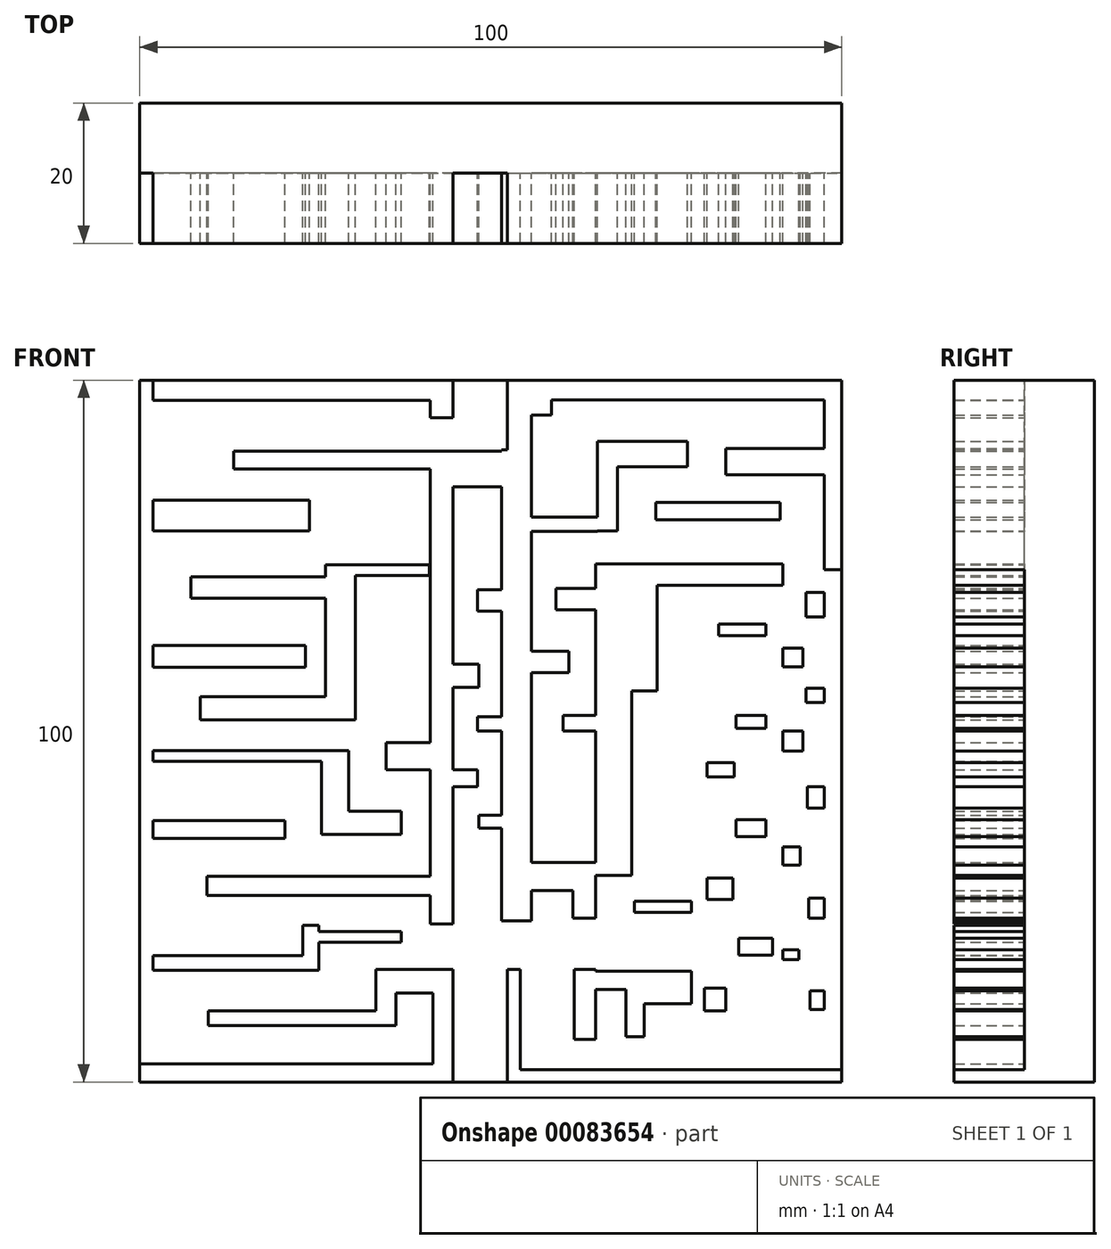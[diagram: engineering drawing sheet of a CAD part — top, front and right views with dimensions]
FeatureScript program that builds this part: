
annotation { "Feature Type Name" : "Feature", "Feature Type Description" : "" }
export const myFeature = defineFeature(function(context is Context, id is Id, definition is map)
    precondition{}
    {
        {
            var Q0;
            Q0=qCreatedBy(makeId("Front.planeOp"),FACE);
            var sketch = newSketch(context, id + "F0", { "sketchPlane" : qUnion([Q0])});
            skLineSegment(sketch, "E0.bottom", {"start": v(50, 50) * mm, "end": v(-50, 50) * mm});
            skLineSegment(sketch, "E0.top", {"start": v(50, -50) * mm, "end": v(-50, -50) * mm});
            skLineSegment(sketch, "E0.left", {"start": v(50, 50) * mm, "end": v(50, -50) * mm});
            skLineSegment(sketch, "E0.right", {"start": v(-50, 50) * mm, "end": v(-50, -50) * mm});
            skPoint(sketch, "E0.middle", {"position": v(0, 0) * mm});
            skSolve(sketch);
        }
        {
            var Q0;
            Q0=makeQuery(id+"F0.imprint","IMPRINT",FACE,{"disambiguationData":[TD([[makeQuery(id+"F0.imprint","IMPRINT",EDGE,{"derivedFrom":sQuery(id+"F0.wireOp",EDGE,"E0.bottom")}),1.0]])]});
            extrude(context, id + "F1", {"entities" : qUnion([Q0]), "depth" : 10 * mm});
        }
        {
            var Q0;
            Q0=makeQuery(id+"F1.opExtrude","CAP_FACE",FACE,{"disambiguationData":[OSD([sQuery(id+"F0.wireOp",EDGE,"E0.bottom"),sQuery(id+"F0.wireOp",EDGE,"E0.top"),sQuery(id+"F0.wireOp",EDGE,"E0.left"),sQuery(id+"F0.wireOp",EDGE,"E0.right")])],"isStart":false});
            var sketch = newSketch(context, id + "F2", { "sketchPlane" : qUnion([Q0])});
            skLineSegment(sketch, "E1.bottom", {"start": v(-5.4, -50) * mm, "end": v(-8.24, -50) * mm});
            skLineSegment(sketch, "E1.top", {"start": v(-5.4, -33.98) * mm, "end": v(-8.24, -33.98) * mm});
            skLineSegment(sketch, "E1.left", {"start": v(-5.4, -50) * mm, "end": v(-5.4, -33.98) * mm});
            skLineSegment(sketch, "E1.right", {"start": v(-8.24, -50) * mm, "end": v(-8.24, -33.98) * mm});
            skLineSegment(sketch, "E2.bottom", {"start": v(2.34, -50) * mm, "end": v(4.17, -50) * mm});
            skLineSegment(sketch, "E2.top", {"start": v(2.34, -33.98) * mm, "end": v(4.17, -33.98) * mm});
            skLineSegment(sketch, "E2.left", {"start": v(2.34, -50) * mm, "end": v(2.34, -33.98) * mm});
            skLineSegment(sketch, "E2.right", {"start": v(4.17, -50) * mm, "end": v(4.17, -33.98) * mm});
            skLineSegment(sketch, "E3.bottom", {"start": v(-5.4, -27.47) * mm, "end": v(-8.65, -27.47) * mm});
            skLineSegment(sketch, "E3.top", {"start": v(-5.4, 39.88) * mm, "end": v(-8.65, 39.88) * mm});
            skLineSegment(sketch, "E3.left", {"start": v(-5.4, -27.47) * mm, "end": v(-5.4, 39.88) * mm});
            skLineSegment(sketch, "E3.right", {"start": v(-8.65, -27.47) * mm, "end": v(-8.65, 39.88) * mm});
            skLineSegment(sketch, "E4.bottom", {"start": v(1.53, -27.06) * mm, "end": v(5.8, -27.06) * mm});
            skLineSegment(sketch, "E4.top", {"start": v(1.53, 40.09) * mm, "end": v(5.8, 40.09) * mm});
            skLineSegment(sketch, "E4.left", {"start": v(1.53, -27.06) * mm, "end": v(1.53, 40.09) * mm});
            skLineSegment(sketch, "E4.right", {"start": v(5.8, -27.06) * mm, "end": v(5.8, 40.09) * mm});
            skLineSegment(sketch, "E5.bottom", {"start": v(1.53, -13.84) * mm, "end": v(-1.73, -13.84) * mm});
            skLineSegment(sketch, "E5.top", {"start": v(1.53, -12) * mm, "end": v(-1.73, -12) * mm});
            skLineSegment(sketch, "E5.left", {"start": v(1.53, -13.84) * mm, "end": v(1.53, -12) * mm});
            skLineSegment(sketch, "E5.right", {"start": v(-1.73, -13.84) * mm, "end": v(-1.73, -12) * mm});
            skLineSegment(sketch, "E6.bottom", {"start": v(-5.4, -5.5) * mm, "end": v(-1.93, -5.5) * mm});
            skLineSegment(sketch, "E6.top", {"start": v(-5.4, -7.94) * mm, "end": v(-1.93, -7.94) * mm});
            skLineSegment(sketch, "E6.left", {"start": v(-5.4, -5.5) * mm, "end": v(-5.4, -7.94) * mm});
            skLineSegment(sketch, "E6.right", {"start": v(-1.93, -5.5) * mm, "end": v(-1.93, -7.94) * mm});
            skLineSegment(sketch, "E7.bottom", {"start": v(1.53, 0) * mm, "end": v(-1.93, 0) * mm});
            skLineSegment(sketch, "E7.top", {"start": v(1.53, 2.03) * mm, "end": v(-1.93, 2.03) * mm});
            skLineSegment(sketch, "E7.left", {"start": v(1.53, 0) * mm, "end": v(1.53, 2.03) * mm});
            skLineSegment(sketch, "E7.right", {"start": v(-1.93, 0) * mm, "end": v(-1.93, 2.03) * mm});
            skLineSegment(sketch, "E8.bottom", {"start": v(-5.4, 6.2) * mm, "end": v(-1.73, 6.2) * mm});
            skLineSegment(sketch, "E8.top", {"start": v(-5.4, 9.56) * mm, "end": v(-1.73, 9.56) * mm});
            skLineSegment(sketch, "E8.left", {"start": v(-5.4, 6.2) * mm, "end": v(-5.4, 9.56) * mm});
            skLineSegment(sketch, "E8.right", {"start": v(-1.73, 6.2) * mm, "end": v(-1.73, 9.56) * mm});
            skLineSegment(sketch, "E9.bottom", {"start": v(1.53, 17.1) * mm, "end": v(-1.93, 17.1) * mm});
            skLineSegment(sketch, "E9.top", {"start": v(1.53, 20.15) * mm, "end": v(-1.93, 20.15) * mm});
            skLineSegment(sketch, "E9.left", {"start": v(1.53, 17.1) * mm, "end": v(1.53, 20.15) * mm});
            skLineSegment(sketch, "E9.right", {"start": v(-1.93, 17.1) * mm, "end": v(-1.93, 20.15) * mm});
            skLineSegment(sketch, "E10.bottom", {"start": v(-5.4, 39.88) * mm, "end": v(1.53, 39.88) * mm});
            skLineSegment(sketch, "E10.top", {"start": v(-5.4, 34.8) * mm, "end": v(1.53, 34.8) * mm});
            skLineSegment(sketch, "E10.left", {"start": v(-5.4, 39.88) * mm, "end": v(-5.4, 34.8) * mm});
            skLineSegment(sketch, "E10.right", {"start": v(1.53, 39.88) * mm, "end": v(1.53, 34.8) * mm});
            skLineSegment(sketch, "E11.bottom", {"start": v(11.9, -33.98) * mm, "end": v(14.96, -33.98) * mm});
            skLineSegment(sketch, "E11.top", {"start": v(11.9, -43.95) * mm, "end": v(14.96, -43.95) * mm});
            skLineSegment(sketch, "E11.left", {"start": v(11.9, -33.98) * mm, "end": v(11.9, -43.95) * mm});
            skLineSegment(sketch, "E11.right", {"start": v(14.96, -33.98) * mm, "end": v(14.96, -43.95) * mm});
            skLineSegment(sketch, "E12.bottom", {"start": v(4.17, -50) * mm, "end": v(21.87, -50) * mm});
            skLineSegment(sketch, "E12.top", {"start": v(4.17, -48.23) * mm, "end": v(21.87, -48.23) * mm});
            skLineSegment(sketch, "E12.left", {"start": v(4.17, -50) * mm, "end": v(4.17, -48.23) * mm});
            skLineSegment(sketch, "E12.right", {"start": v(21.87, -50) * mm, "end": v(21.87, -48.23) * mm});
            skLineSegment(sketch, "E13.bottom", {"start": v(11.7, -26.66) * mm, "end": v(14.96, -26.66) * mm});
            skLineSegment(sketch, "E13.top", {"start": v(11.7, -18.72) * mm, "end": v(14.96, -18.72) * mm});
            skLineSegment(sketch, "E13.left", {"start": v(11.7, -26.66) * mm, "end": v(11.7, -18.72) * mm});
            skLineSegment(sketch, "E13.right", {"start": v(14.96, -26.66) * mm, "end": v(14.96, -18.72) * mm});
            skLineSegment(sketch, "E14.bottom", {"start": v(11.7, -18.72) * mm, "end": v(5.8, -18.72) * mm});
            skLineSegment(sketch, "E14.top", {"start": v(11.7, -22.69) * mm, "end": v(5.8, -22.69) * mm});
            skLineSegment(sketch, "E14.left", {"start": v(11.7, -18.72) * mm, "end": v(11.7, -22.69) * mm});
            skLineSegment(sketch, "E14.right", {"start": v(5.8, -18.72) * mm, "end": v(5.8, -22.69) * mm});
            skLineSegment(sketch, "E15.bottom", {"start": v(21.87, -43.55) * mm, "end": v(19.23, -43.55) * mm});
            skLineSegment(sketch, "E15.top", {"start": v(21.87, -34.19) * mm, "end": v(19.23, -34.19) * mm});
            skLineSegment(sketch, "E15.left", {"start": v(21.87, -43.55) * mm, "end": v(21.87, -34.19) * mm});
            skLineSegment(sketch, "E15.right", {"start": v(19.23, -43.55) * mm, "end": v(19.23, -34.19) * mm});
            skLineSegment(sketch, "E16.bottom", {"start": v(19.23, -34.19) * mm, "end": v(14.96, -34.19) * mm});
            skLineSegment(sketch, "E16.top", {"start": v(19.23, -36.83) * mm, "end": v(14.96, -36.83) * mm});
            skLineSegment(sketch, "E16.left", {"start": v(19.23, -34.19) * mm, "end": v(19.23, -36.83) * mm});
            skLineSegment(sketch, "E16.right", {"start": v(14.96, -34.19) * mm, "end": v(14.96, -36.83) * mm});
            skLineSegment(sketch, "E17.bottom", {"start": v(21.87, -50) * mm, "end": v(50, -50) * mm});
            skLineSegment(sketch, "E17.top", {"start": v(21.87, -48.23) * mm, "end": v(50, -48.23) * mm});
            skLineSegment(sketch, "E17.right", {"start": v(50, -50) * mm, "end": v(50, -48.23) * mm});
            skLineSegment(sketch, "E18.bottom", {"start": v(28.6, -48.23) * mm, "end": v(30.83, -48.23) * mm});
            skLineSegment(sketch, "E18.top", {"start": v(28.6, 6.1) * mm, "end": v(30.83, 6.1) * mm});
            skLineSegment(sketch, "E18.left", {"start": v(28.6, -48.23) * mm, "end": v(28.6, 6.1) * mm});
            skLineSegment(sketch, "E18.right", {"start": v(30.83, -48.23) * mm, "end": v(30.83, 6.1) * mm});
            skLineSegment(sketch, "E19.bottom", {"start": v(21.87, -34.19) * mm, "end": v(28.6, -34.19) * mm});
            skLineSegment(sketch, "E19.top", {"start": v(21.87, -38.87) * mm, "end": v(28.6, -38.87) * mm});
            skLineSegment(sketch, "E19.left", {"start": v(21.87, -34.19) * mm, "end": v(21.87, -38.87) * mm});
            skLineSegment(sketch, "E19.right", {"start": v(28.6, -34.19) * mm, "end": v(28.6, -38.87) * mm});
            skLineSegment(sketch, "E20.bottom", {"start": v(28.6, -24.22) * mm, "end": v(20.45, -24.22) * mm});
            skLineSegment(sketch, "E20.top", {"start": v(28.6, -25.84) * mm, "end": v(20.45, -25.84) * mm});
            skLineSegment(sketch, "E20.left", {"start": v(28.6, -24.22) * mm, "end": v(28.6, -25.84) * mm});
            skLineSegment(sketch, "E20.right", {"start": v(20.45, -24.22) * mm, "end": v(20.45, -25.84) * mm});
            skLineSegment(sketch, "E21.bottom", {"start": v(14.96, -18.72) * mm, "end": v(20.04, -18.72) * mm});
            skLineSegment(sketch, "E21.top", {"start": v(14.96, 5.7) * mm, "end": v(20.04, 5.7) * mm});
            skLineSegment(sketch, "E21.left", {"start": v(14.96, -18.72) * mm, "end": v(14.96, 5.7) * mm});
            skLineSegment(sketch, "E21.right", {"start": v(20.04, -18.72) * mm, "end": v(20.04, 5.7) * mm});
            skLineSegment(sketch, "E22.bottom", {"start": v(14.96, 5.7) * mm, "end": v(23.7, 5.7) * mm});
            skLineSegment(sketch, "E22.top", {"start": v(14.96, 23.8) * mm, "end": v(23.7, 23.8) * mm});
            skLineSegment(sketch, "E22.left", {"start": v(14.96, 5.7) * mm, "end": v(14.96, 23.8) * mm});
            skLineSegment(sketch, "E22.right", {"start": v(23.7, 5.7) * mm, "end": v(23.7, 23.8) * mm});
            skLineSegment(sketch, "E23.bottom", {"start": v(23.7, 23.8) * mm, "end": v(41.61, 23.8) * mm});
            skLineSegment(sketch, "E23.top", {"start": v(23.7, 20.76) * mm, "end": v(41.61, 20.76) * mm});
            skLineSegment(sketch, "E23.left", {"start": v(23.7, 23.8) * mm, "end": v(23.7, 20.76) * mm});
            skLineSegment(sketch, "E23.right", {"start": v(41.61, 23.8) * mm, "end": v(41.61, 20.76) * mm});
            skLineSegment(sketch, "E24.bottom", {"start": v(41.61, 20.76) * mm, "end": v(39.17, 20.76) * mm});
            skLineSegment(sketch, "E24.top", {"start": v(41.61, -41.92) * mm, "end": v(39.17, -41.92) * mm});
            skLineSegment(sketch, "E24.left", {"start": v(41.61, 20.76) * mm, "end": v(41.61, -41.92) * mm});
            skLineSegment(sketch, "E24.right", {"start": v(39.17, 20.76) * mm, "end": v(39.17, -41.92) * mm});
            skLineSegment(sketch, "E25.bottom", {"start": v(39.17, 13.63) * mm, "end": v(32.46, 13.63) * mm});
            skLineSegment(sketch, "E25.top", {"start": v(39.17, 15.26) * mm, "end": v(32.46, 15.26) * mm});
            skLineSegment(sketch, "E25.left", {"start": v(39.17, 13.63) * mm, "end": v(39.17, 15.26) * mm});
            skLineSegment(sketch, "E25.right", {"start": v(32.46, 13.63) * mm, "end": v(32.46, 15.26) * mm});
            skLineSegment(sketch, "E26.bottom", {"start": v(39.17, 0.4) * mm, "end": v(34.9, 0.4) * mm});
            skLineSegment(sketch, "E26.top", {"start": v(39.17, 2.24) * mm, "end": v(34.9, 2.24) * mm});
            skLineSegment(sketch, "E26.left", {"start": v(39.17, 0.4) * mm, "end": v(39.17, 2.24) * mm});
            skLineSegment(sketch, "E26.right", {"start": v(34.9, 0.4) * mm, "end": v(34.9, 2.24) * mm});
            skLineSegment(sketch, "E27.bottom", {"start": v(30.83, -6.51) * mm, "end": v(34.7, -6.51) * mm});
            skLineSegment(sketch, "E27.top", {"start": v(30.83, -4.48) * mm, "end": v(34.7, -4.48) * mm});
            skLineSegment(sketch, "E27.left", {"start": v(30.83, -6.51) * mm, "end": v(30.83, -4.48) * mm});
            skLineSegment(sketch, "E27.right", {"start": v(34.7, -6.51) * mm, "end": v(34.7, -4.48) * mm});
            skLineSegment(sketch, "E28.bottom", {"start": v(39.17, -15.06) * mm, "end": v(34.9, -15.06) * mm});
            skLineSegment(sketch, "E28.top", {"start": v(39.17, -12.62) * mm, "end": v(34.9, -12.62) * mm});
            skLineSegment(sketch, "E28.left", {"start": v(39.17, -15.06) * mm, "end": v(39.17, -12.62) * mm});
            skLineSegment(sketch, "E28.right", {"start": v(34.9, -15.06) * mm, "end": v(34.9, -12.62) * mm});
            skLineSegment(sketch, "E29.bottom", {"start": v(30.83, -24.01) * mm, "end": v(34.5, -24.01) * mm});
            skLineSegment(sketch, "E29.top", {"start": v(30.83, -20.96) * mm, "end": v(34.5, -20.96) * mm});
            skLineSegment(sketch, "E29.left", {"start": v(30.83, -24.01) * mm, "end": v(30.83, -20.96) * mm});
            skLineSegment(sketch, "E29.right", {"start": v(34.5, -24.01) * mm, "end": v(34.5, -20.96) * mm});
            skLineSegment(sketch, "E30.bottom", {"start": v(40.14, -31.95) * mm, "end": v(35.3, -31.95) * mm});
            skLineSegment(sketch, "E30.top", {"start": v(40.14, -29.5) * mm, "end": v(35.3, -29.5) * mm});
            skLineSegment(sketch, "E30.left", {"start": v(40.14, -31.95) * mm, "end": v(40.14, -29.5) * mm});
            skLineSegment(sketch, "E30.right", {"start": v(35.3, -31.95) * mm, "end": v(35.3, -29.5) * mm});
            skLineSegment(sketch, "E31.bottom", {"start": v(30.42, -39.88) * mm, "end": v(33.47, -39.88) * mm});
            skLineSegment(sketch, "E31.top", {"start": v(30.42, -36.63) * mm, "end": v(33.47, -36.63) * mm});
            skLineSegment(sketch, "E31.left", {"start": v(30.42, -39.88) * mm, "end": v(30.42, -36.63) * mm});
            skLineSegment(sketch, "E31.right", {"start": v(33.47, -39.88) * mm, "end": v(33.47, -36.63) * mm});
            skLineSegment(sketch, "E32.bottom", {"start": v(50, -48.23) * mm, "end": v(47.51, -48.23) * mm});
            skLineSegment(sketch, "E32.top", {"start": v(50, 23) * mm, "end": v(47.51, 23) * mm});
            skLineSegment(sketch, "E32.left", {"start": v(50, -48.23) * mm, "end": v(50, 23) * mm});
            skLineSegment(sketch, "E32.right", {"start": v(47.51, -48.23) * mm, "end": v(47.51, 23) * mm});
            skLineSegment(sketch, "E33.top", {"start": v(50, 50) * mm, "end": v(47.51, 50) * mm});
            skLineSegment(sketch, "E33.left", {"start": v(50, 23) * mm, "end": v(50, 50) * mm});
            skLineSegment(sketch, "E33.right", {"start": v(47.51, 23) * mm, "end": v(47.51, 50) * mm});
            skLineSegment(sketch, "E34.bottom", {"start": v(47.51, -37.03) * mm, "end": v(45.48, -37.03) * mm});
            skLineSegment(sketch, "E34.top", {"start": v(47.51, -39.68) * mm, "end": v(45.48, -39.68) * mm});
            skLineSegment(sketch, "E34.left", {"start": v(47.51, -37.03) * mm, "end": v(47.51, -39.68) * mm});
            skLineSegment(sketch, "E34.right", {"start": v(45.48, -37.03) * mm, "end": v(45.48, -39.68) * mm});
            skLineSegment(sketch, "E35.bottom", {"start": v(41.61, -32.56) * mm, "end": v(43.85, -32.56) * mm});
            skLineSegment(sketch, "E35.top", {"start": v(41.61, -31.13) * mm, "end": v(43.85, -31.13) * mm});
            skLineSegment(sketch, "E35.left", {"start": v(41.61, -32.56) * mm, "end": v(41.61, -31.13) * mm});
            skLineSegment(sketch, "E35.right", {"start": v(43.85, -32.56) * mm, "end": v(43.85, -31.13) * mm});
            skLineSegment(sketch, "E36.bottom", {"start": v(47.51, -26.66) * mm, "end": v(45.28, -26.66) * mm});
            skLineSegment(sketch, "E36.top", {"start": v(47.51, -23.8) * mm, "end": v(45.28, -23.8) * mm});
            skLineSegment(sketch, "E36.left", {"start": v(47.51, -26.66) * mm, "end": v(47.51, -23.8) * mm});
            skLineSegment(sketch, "E36.right", {"start": v(45.28, -26.66) * mm, "end": v(45.28, -23.8) * mm});
            skLineSegment(sketch, "E37.bottom", {"start": v(41.61, -19.13) * mm, "end": v(44.06, -19.13) * mm});
            skLineSegment(sketch, "E37.top", {"start": v(41.61, -16.48) * mm, "end": v(44.06, -16.48) * mm});
            skLineSegment(sketch, "E37.left", {"start": v(41.61, -19.13) * mm, "end": v(41.61, -16.48) * mm});
            skLineSegment(sketch, "E37.right", {"start": v(44.06, -19.13) * mm, "end": v(44.06, -16.48) * mm});
            skLineSegment(sketch, "E38.bottom", {"start": v(47.51, -10.99) * mm, "end": v(45.07, -10.99) * mm});
            skLineSegment(sketch, "E38.top", {"start": v(47.51, -7.94) * mm, "end": v(45.07, -7.94) * mm});
            skLineSegment(sketch, "E38.left", {"start": v(47.51, -10.99) * mm, "end": v(47.51, -7.94) * mm});
            skLineSegment(sketch, "E38.right", {"start": v(45.07, -10.99) * mm, "end": v(45.07, -7.94) * mm});
            skLineSegment(sketch, "E39.bottom", {"start": v(41.61, -2.85) * mm, "end": v(44.46, -2.85) * mm});
            skLineSegment(sketch, "E39.top", {"start": v(41.61, 0) * mm, "end": v(44.46, 0) * mm});
            skLineSegment(sketch, "E39.left", {"start": v(41.61, -2.85) * mm, "end": v(41.61, 0) * mm});
            skLineSegment(sketch, "E39.right", {"start": v(44.46, -2.85) * mm, "end": v(44.46, 0) * mm});
            skLineSegment(sketch, "E40.bottom", {"start": v(47.51, 6.1) * mm, "end": v(44.87, 6.1) * mm});
            skLineSegment(sketch, "E40.top", {"start": v(47.51, 4.07) * mm, "end": v(44.87, 4.07) * mm});
            skLineSegment(sketch, "E40.left", {"start": v(47.51, 6.1) * mm, "end": v(47.51, 4.07) * mm});
            skLineSegment(sketch, "E40.right", {"start": v(44.87, 6.1) * mm, "end": v(44.87, 4.07) * mm});
            skLineSegment(sketch, "E41.bottom", {"start": v(41.61, 9.16) * mm, "end": v(44.46, 9.16) * mm});
            skLineSegment(sketch, "E41.top", {"start": v(41.61, 11.8) * mm, "end": v(44.46, 11.8) * mm});
            skLineSegment(sketch, "E41.left", {"start": v(41.61, 9.16) * mm, "end": v(41.61, 11.8) * mm});
            skLineSegment(sketch, "E41.right", {"start": v(44.46, 9.16) * mm, "end": v(44.46, 11.8) * mm});
            skLineSegment(sketch, "E42.bottom", {"start": v(47.51, 16.28) * mm, "end": v(44.87, 16.28) * mm});
            skLineSegment(sketch, "E42.top", {"start": v(47.51, 19.74) * mm, "end": v(44.87, 19.74) * mm});
            skLineSegment(sketch, "E42.left", {"start": v(47.51, 16.28) * mm, "end": v(47.51, 19.74) * mm});
            skLineSegment(sketch, "E42.right", {"start": v(44.87, 16.28) * mm, "end": v(44.87, 19.74) * mm});
            skLineSegment(sketch, "E43.bottom", {"start": v(41.2, 30.12) * mm, "end": v(23.5, 30.12) * mm});
            skLineSegment(sketch, "E43.top", {"start": v(41.2, 32.56) * mm, "end": v(23.5, 32.56) * mm});
            skLineSegment(sketch, "E43.left", {"start": v(41.2, 30.12) * mm, "end": v(41.2, 32.56) * mm});
            skLineSegment(sketch, "E43.right", {"start": v(23.5, 30.12) * mm, "end": v(23.5, 32.56) * mm});
            skLineSegment(sketch, "E44.bottom", {"start": v(18, 30.52) * mm, "end": v(15.16, 30.52) * mm});
            skLineSegment(sketch, "E44.top", {"start": v(18, 41.3) * mm, "end": v(15.16, 41.3) * mm});
            skLineSegment(sketch, "E44.left", {"start": v(18, 30.52) * mm, "end": v(18, 41.3) * mm});
            skLineSegment(sketch, "E44.right", {"start": v(15.16, 30.52) * mm, "end": v(15.16, 41.3) * mm});
            skLineSegment(sketch, "E45.bottom", {"start": v(18, 41.3) * mm, "end": v(27.98, 41.3) * mm});
            skLineSegment(sketch, "E45.top", {"start": v(18, 37.65) * mm, "end": v(27.98, 37.65) * mm});
            skLineSegment(sketch, "E45.left", {"start": v(18, 41.3) * mm, "end": v(18, 37.65) * mm});
            skLineSegment(sketch, "E45.right", {"start": v(27.98, 41.3) * mm, "end": v(27.98, 37.65) * mm});
            skLineSegment(sketch, "E46.bottom", {"start": v(27.98, 37.65) * mm, "end": v(26.35, 37.65) * mm});
            skLineSegment(sketch, "E46.top", {"start": v(27.98, 32.56) * mm, "end": v(26.35, 32.56) * mm});
            skLineSegment(sketch, "E46.left", {"start": v(27.98, 37.65) * mm, "end": v(27.98, 32.56) * mm});
            skLineSegment(sketch, "E46.right", {"start": v(26.35, 37.65) * mm, "end": v(26.35, 32.56) * mm});
            skLineSegment(sketch, "E47.bottom", {"start": v(15.16, 30.52) * mm, "end": v(5.8, 30.52) * mm});
            skLineSegment(sketch, "E47.top", {"start": v(15.16, 28.49) * mm, "end": v(5.8, 28.49) * mm});
            skLineSegment(sketch, "E47.left", {"start": v(15.16, 30.52) * mm, "end": v(15.16, 28.49) * mm});
            skLineSegment(sketch, "E47.right", {"start": v(5.8, 30.52) * mm, "end": v(5.8, 28.49) * mm});
            skLineSegment(sketch, "E48.bottom", {"start": v(14.96, 20.35) * mm, "end": v(9.26, 20.35) * mm});
            skLineSegment(sketch, "E48.top", {"start": v(14.96, 17.3) * mm, "end": v(9.26, 17.3) * mm});
            skLineSegment(sketch, "E48.left", {"start": v(14.96, 20.35) * mm, "end": v(14.96, 17.3) * mm});
            skLineSegment(sketch, "E48.right", {"start": v(9.26, 20.35) * mm, "end": v(9.26, 17.3) * mm});
            skLineSegment(sketch, "E49.bottom", {"start": v(5.8, 11.4) * mm, "end": v(11.1, 11.4) * mm});
            skLineSegment(sketch, "E49.top", {"start": v(5.8, 8.34) * mm, "end": v(11.1, 8.34) * mm});
            skLineSegment(sketch, "E49.left", {"start": v(5.8, 11.4) * mm, "end": v(5.8, 8.34) * mm});
            skLineSegment(sketch, "E49.right", {"start": v(11.1, 11.4) * mm, "end": v(11.1, 8.34) * mm});
            skLineSegment(sketch, "E50.bottom", {"start": v(14.96, 0) * mm, "end": v(10.28, 0) * mm});
            skLineSegment(sketch, "E50.top", {"start": v(14.96, 2.24) * mm, "end": v(10.28, 2.24) * mm});
            skLineSegment(sketch, "E50.left", {"start": v(14.96, 0) * mm, "end": v(14.96, 2.24) * mm});
            skLineSegment(sketch, "E50.right", {"start": v(10.28, 0) * mm, "end": v(10.28, 2.24) * mm});
            skLineSegment(sketch, "E51.bottom", {"start": v(47.51, 40.3) * mm, "end": v(33.47, 40.3) * mm});
            skLineSegment(sketch, "E51.top", {"start": v(47.51, 36.5) * mm, "end": v(33.47, 36.5) * mm});
            skLineSegment(sketch, "E51.left", {"start": v(47.51, 40.3) * mm, "end": v(47.51, 36.5) * mm});
            skLineSegment(sketch, "E51.right", {"start": v(33.47, 40.3) * mm, "end": v(33.47, 36.5) * mm});
            skLineSegment(sketch, "E52.bottom", {"start": v(47.51, 50) * mm, "end": v(8.65, 50) * mm});
            skLineSegment(sketch, "E52.top", {"start": v(47.51, 47.2) * mm, "end": v(8.65, 47.2) * mm});
            skLineSegment(sketch, "E52.left", {"start": v(47.51, 50) * mm, "end": v(47.51, 47.2) * mm});
            skLineSegment(sketch, "E52.right", {"start": v(8.65, 50) * mm, "end": v(8.65, 47.2) * mm});
            skLineSegment(sketch, "E53.bottom", {"start": v(2.34, 50) * mm, "end": v(5.8, 50) * mm});
            skLineSegment(sketch, "E53.top", {"start": v(2.34, 40.09) * mm, "end": v(5.8, 40.09) * mm});
            skLineSegment(sketch, "E53.left", {"start": v(2.34, 50) * mm, "end": v(2.34, 40.09) * mm});
            skLineSegment(sketch, "E53.right", {"start": v(5.8, 50) * mm, "end": v(5.8, 40.09) * mm});
            skLineSegment(sketch, "E54.bottom", {"start": v(8.65, 50) * mm, "end": v(5.8, 50) * mm});
            skLineSegment(sketch, "E54.top", {"start": v(8.65, 45.04) * mm, "end": v(5.8, 45.04) * mm});
            skLineSegment(sketch, "E54.left", {"start": v(8.65, 50) * mm, "end": v(8.65, 45.04) * mm});
            skLineSegment(sketch, "E54.right", {"start": v(5.8, 50) * mm, "end": v(5.8, 45.04) * mm});
            skLineSegment(sketch, "E55.bottom", {"start": v(-8.24, -50) * mm, "end": v(-50, -50) * mm});
            skLineSegment(sketch, "E55.top", {"start": v(-8.24, -47.41) * mm, "end": v(-50, -47.41) * mm});
            skLineSegment(sketch, "E55.left", {"start": v(-8.24, -50) * mm, "end": v(-8.24, -47.41) * mm});
            skLineSegment(sketch, "E55.right", {"start": v(-50, -50) * mm, "end": v(-50, -47.41) * mm});
            skLineSegment(sketch, "E56.bottom", {"start": v(-50, -47.41) * mm, "end": v(-48.13, -47.41) * mm});
            skLineSegment(sketch, "E56.top", {"start": v(-50, 50) * mm, "end": v(-48.13, 50) * mm});
            skLineSegment(sketch, "E56.left", {"start": v(-50, -47.41) * mm, "end": v(-50, 50) * mm});
            skLineSegment(sketch, "E56.right", {"start": v(-48.13, -47.41) * mm, "end": v(-48.13, 50) * mm});
            skPoint(sketch, "E57.oppositeSnap0", {"position": v(-8.24, -42) * mm});
            skLineSegment(sketch, "E57.bottom", {"start": v(-13.53, -33.98) * mm, "end": v(-16.38, -33.98) * mm});
            skLineSegment(sketch, "E57.top", {"start": v(-13.53, -42) * mm, "end": v(-16.38, -42) * mm});
            skLineSegment(sketch, "E57.left", {"start": v(-13.53, -33.98) * mm, "end": v(-13.53, -42) * mm});
            skLineSegment(sketch, "E57.right", {"start": v(-16.38, -33.98) * mm, "end": v(-16.38, -42) * mm});
            skLineSegment(sketch, "E58.bottom", {"start": v(-16.38, -42) * mm, "end": v(-40.25, -42) * mm});
            skLineSegment(sketch, "E58.top", {"start": v(-16.38, -39.86) * mm, "end": v(-40.25, -39.86) * mm});
            skLineSegment(sketch, "E58.left", {"start": v(-16.38, -42) * mm, "end": v(-16.38, -39.86) * mm});
            skLineSegment(sketch, "E58.right", {"start": v(-40.25, -42) * mm, "end": v(-40.25, -39.86) * mm});
            skLineSegment(sketch, "E59.bottom", {"start": v(-48.13, -31.99) * mm, "end": v(-26.8, -31.99) * mm});
            skLineSegment(sketch, "E59.top", {"start": v(-48.13, -34.1) * mm, "end": v(-26.8, -34.1) * mm});
            skLineSegment(sketch, "E59.left", {"start": v(-48.13, -31.99) * mm, "end": v(-48.13, -34.1) * mm});
            skLineSegment(sketch, "E60.top", {"start": v(-26.8, -27.68) * mm, "end": v(-24.5, -27.68) * mm});
            skLineSegment(sketch, "E60.left", {"start": v(-26.8, -31.99) * mm, "end": v(-26.8, -27.68) * mm});
            skLineSegment(sketch, "E60.right", {"start": v(-24.5, -31.99) * mm, "end": v(-24.5, -30.07) * mm});
            skLineSegment(sketch, "E61.bottom", {"start": v(-24.5, -28.53) * mm, "end": v(-12.79, -28.53) * mm});
            skLineSegment(sketch, "E61.top", {"start": v(-24.5, -30.07) * mm, "end": v(-12.79, -30.07) * mm});
            skLineSegment(sketch, "E61.right", {"start": v(-12.79, -28.53) * mm, "end": v(-12.79, -30.07) * mm});
            skLineSegment(sketch, "E62.bottom", {"start": v(-8.65, -20.66) * mm, "end": v(-40.44, -20.66) * mm});
            skLineSegment(sketch, "E62.top", {"start": v(-8.65, -23.44) * mm, "end": v(-40.44, -23.44) * mm});
            skLineSegment(sketch, "E62.left", {"start": v(-8.65, -20.66) * mm, "end": v(-8.65, -23.44) * mm});
            skLineSegment(sketch, "E62.right", {"start": v(-40.44, -20.66) * mm, "end": v(-40.44, -23.44) * mm});
            skLineSegment(sketch, "E63.bottom", {"start": v(-48.13, -12.78) * mm, "end": v(-29.3, -12.78) * mm});
            skLineSegment(sketch, "E63.top", {"start": v(-48.13, -15.28) * mm, "end": v(-29.3, -15.28) * mm});
            skLineSegment(sketch, "E63.left", {"start": v(-48.13, -12.78) * mm, "end": v(-48.13, -15.28) * mm});
            skLineSegment(sketch, "E63.right", {"start": v(-29.3, -12.78) * mm, "end": v(-29.3, -15.28) * mm});
            skLineSegment(sketch, "E64.bottom", {"start": v(-24.12, -14.7) * mm, "end": v(-20.28, -14.7) * mm});
            skLineSegment(sketch, "E64.top", {"start": v(-24.12, -2.8) * mm, "end": v(-20.28, -2.8) * mm});
            skLineSegment(sketch, "E64.left", {"start": v(-24.12, -14.7) * mm, "end": v(-24.12, -2.8) * mm});
            skLineSegment(sketch, "E64.right", {"start": v(-20.28, -14.7) * mm, "end": v(-20.28, -2.8) * mm});
            skLineSegment(sketch, "E65.bottom", {"start": v(-24.12, -2.8) * mm, "end": v(-48.13, -2.8) * mm});
            skLineSegment(sketch, "E65.top", {"start": v(-24.12, -4.33) * mm, "end": v(-48.13, -4.33) * mm});
            skLineSegment(sketch, "E65.left", {"start": v(-24.12, -2.8) * mm, "end": v(-24.12, -4.33) * mm});
            skLineSegment(sketch, "E65.right", {"start": v(-48.13, -2.8) * mm, "end": v(-48.13, -4.33) * mm});
            skLineSegment(sketch, "E66.bottom", {"start": v(-20.28, -14.7) * mm, "end": v(-12.79, -14.7) * mm});
            skLineSegment(sketch, "E66.top", {"start": v(-20.28, -11.44) * mm, "end": v(-12.79, -11.44) * mm});
            skLineSegment(sketch, "E66.left", {"start": v(-20.28, -14.7) * mm, "end": v(-20.28, -11.44) * mm});
            skLineSegment(sketch, "E66.right", {"start": v(-12.79, -14.7) * mm, "end": v(-12.79, -11.44) * mm});
            skLineSegment(sketch, "E67.bottom", {"start": v(-8.65, -1.64) * mm, "end": v(-14.9, -1.64) * mm});
            skLineSegment(sketch, "E67.top", {"start": v(-8.65, -5.48) * mm, "end": v(-14.9, -5.48) * mm});
            skLineSegment(sketch, "E67.left", {"start": v(-8.65, -1.64) * mm, "end": v(-8.65, -5.48) * mm});
            skLineSegment(sketch, "E67.right", {"start": v(-14.9, -1.64) * mm, "end": v(-14.9, -5.48) * mm});
            skLineSegment(sketch, "E68.bottom", {"start": v(-14.9, -1.64) * mm, "end": v(-12.98, -1.64) * mm});
            skLineSegment(sketch, "E68.top", {"start": v(-14.9, 17.18) * mm, "end": v(-12.98, 17.18) * mm});
            skLineSegment(sketch, "E68.left", {"start": v(-14.9, -1.64) * mm, "end": v(-14.9, 17.18) * mm});
            skLineSegment(sketch, "E68.right", {"start": v(-12.98, -1.64) * mm, "end": v(-12.98, 17.18) * mm});
            skLineSegment(sketch, "E69.bottom", {"start": v(-8.75, 23.71) * mm, "end": v(-19.32, 23.71) * mm});
            skLineSegment(sketch, "E69.top", {"start": v(-8.75, 22.17) * mm, "end": v(-19.32, 22.17) * mm});
            skLineSegment(sketch, "E69.left", {"start": v(-8.75, 23.71) * mm, "end": v(-8.75, 22.17) * mm});
            skLineSegment(sketch, "E69.right", {"start": v(-19.32, 23.71) * mm, "end": v(-19.32, 22.17) * mm});
            skLineSegment(sketch, "E70.bottom", {"start": v(-19.32, 23.71) * mm, "end": v(-23.54, 23.71) * mm});
            skLineSegment(sketch, "E70.top", {"start": v(-19.32, 4.89) * mm, "end": v(-23.54, 4.89) * mm});
            skLineSegment(sketch, "E70.left", {"start": v(-19.32, 23.71) * mm, "end": v(-19.32, 4.89) * mm});
            skLineSegment(sketch, "E70.right", {"start": v(-23.54, 23.71) * mm, "end": v(-23.54, 4.89) * mm});
            skLineSegment(sketch, "E71.bottom", {"start": v(-23.54, 4.89) * mm, "end": v(-41.4, 4.89) * mm});
            skLineSegment(sketch, "E71.top", {"start": v(-23.54, 1.62) * mm, "end": v(-41.4, 1.62) * mm});
            skLineSegment(sketch, "E71.left", {"start": v(-23.54, 4.89) * mm, "end": v(-23.54, 1.62) * mm});
            skLineSegment(sketch, "E71.right", {"start": v(-41.4, 4.89) * mm, "end": v(-41.4, 1.62) * mm});
            skLineSegment(sketch, "E72.bottom", {"start": v(-48.13, 12.19) * mm, "end": v(-26.42, 12.19) * mm});
            skLineSegment(sketch, "E72.top", {"start": v(-48.13, 9.11) * mm, "end": v(-26.42, 9.11) * mm});
            skLineSegment(sketch, "E72.left", {"start": v(-48.13, 12.19) * mm, "end": v(-48.13, 9.11) * mm});
            skLineSegment(sketch, "E72.right", {"start": v(-26.42, 12.19) * mm, "end": v(-26.42, 9.11) * mm});
            skLineSegment(sketch, "E73.bottom", {"start": v(-23.54, 21.98) * mm, "end": v(-42.75, 21.98) * mm});
            skLineSegment(sketch, "E73.top", {"start": v(-23.54, 18.9) * mm, "end": v(-42.75, 18.9) * mm});
            skLineSegment(sketch, "E73.left", {"start": v(-23.54, 21.98) * mm, "end": v(-23.54, 18.9) * mm});
            skLineSegment(sketch, "E73.right", {"start": v(-42.75, 21.98) * mm, "end": v(-42.75, 18.9) * mm});
            skLineSegment(sketch, "E74.bottom", {"start": v(-48.13, 32.93) * mm, "end": v(-25.85, 32.93) * mm});
            skLineSegment(sketch, "E74.top", {"start": v(-48.13, 28.51) * mm, "end": v(-25.85, 28.51) * mm});
            skLineSegment(sketch, "E74.left", {"start": v(-48.13, 32.93) * mm, "end": v(-48.13, 28.51) * mm});
            skLineSegment(sketch, "E74.right", {"start": v(-25.85, 32.93) * mm, "end": v(-25.85, 28.51) * mm});
            skLineSegment(sketch, "E75.bottom", {"start": v(-5.4, 50) * mm, "end": v(-8.65, 50) * mm});
            skLineSegment(sketch, "E75.top", {"start": v(-5.4, 44.65) * mm, "end": v(-8.65, 44.65) * mm});
            skLineSegment(sketch, "E75.left", {"start": v(-5.4, 50) * mm, "end": v(-5.4, 44.65) * mm});
            skLineSegment(sketch, "E75.right", {"start": v(-8.65, 50) * mm, "end": v(-8.65, 44.65) * mm});
            skLineSegment(sketch, "E76.bottom", {"start": v(-8.65, 50) * mm, "end": v(-48.13, 50) * mm});
            skLineSegment(sketch, "E76.top", {"start": v(-8.65, 47.14) * mm, "end": v(-48.13, 47.14) * mm});
            skLineSegment(sketch, "E76.left", {"start": v(-8.65, 50) * mm, "end": v(-8.65, 47.14) * mm});
            skLineSegment(sketch, "E76.right", {"start": v(-48.13, 50) * mm, "end": v(-48.13, 47.14) * mm});
            skLineSegment(sketch, "E77.bottom", {"start": v(-8.65, 39.88) * mm, "end": v(-36.6, 39.88) * mm});
            skLineSegment(sketch, "E77.top", {"start": v(-8.65, 37.35) * mm, "end": v(-36.6, 37.35) * mm});
            skLineSegment(sketch, "E77.left", {"start": v(-8.65, 39.88) * mm, "end": v(-8.65, 37.35) * mm});
            skLineSegment(sketch, "E77.right", {"start": v(-36.6, 39.88) * mm, "end": v(-36.6, 37.35) * mm});
            skLineSegment(sketch, "E78.bottom", {"start": v(-19.32, 23.71) * mm, "end": v(-15.28, 23.71) * mm});
            skLineSegment(sketch, "E78.top", {"start": v(-19.32, 32.74) * mm, "end": v(-15.28, 32.74) * mm});
            skLineSegment(sketch, "E78.left", {"start": v(-19.32, 23.71) * mm, "end": v(-19.32, 32.74) * mm});
            skLineSegment(sketch, "E78.right", {"start": v(-15.28, 23.71) * mm, "end": v(-15.28, 32.74) * mm});
            skLineSegment(sketch, "E79.bottom", {"start": v(-42.56, 32.93) * mm, "end": v(-41.02, 32.93) * mm});
            skLineSegment(sketch, "E79.top", {"start": v(-42.56, 42.34) * mm, "end": v(-41.02, 42.34) * mm});
            skLineSegment(sketch, "E79.left", {"start": v(-42.56, 32.93) * mm, "end": v(-42.56, 42.34) * mm});
            skLineSegment(sketch, "E79.right", {"start": v(-41.02, 32.93) * mm, "end": v(-41.02, 42.34) * mm});
            skLineSegment(sketch, "E80.bottom", {"start": v(-13.53, -33.98) * mm, "end": v(-8.24, -33.98) * mm});
            skLineSegment(sketch, "E80.top", {"start": v(-13.53, -37.3) * mm, "end": v(-8.24, -37.3) * mm});
            skLineSegment(sketch, "E80.left", {"start": v(-13.53, -33.98) * mm, "end": v(-13.53, -37.3) * mm});
            skLineSegment(sketch, "E80.right", {"start": v(-8.24, -33.98) * mm, "end": v(-8.24, -37.3) * mm});
            skLineSegment(sketch, "E81.bottom", {"start": v(-23.54, 1.62) * mm, "end": v(-19.32, 1.62) * mm});
            skLineSegment(sketch, "E81.top", {"start": v(-23.54, 4.89) * mm, "end": v(-19.32, 4.89) * mm});
            skLineSegment(sketch, "E81.left", {"start": v(-23.54, 1.62) * mm, "end": v(-23.54, 4.89) * mm});
            skLineSegment(sketch, "E81.right", {"start": v(-19.32, 1.62) * mm, "end": v(-19.32, 4.89) * mm});
            skLineSegment(sketch, "E82", {"start": v(-24.5, -31.99) * mm, "end": v(-24.5, -34.1) * mm});
            skLineSegment(sketch, "E83", {"start": v(-24.5, -34.1) * mm, "end": v(-26.8, -34.1) * mm});
            skLineSegment(sketch, "E84.bottom", {"start": v(15.16, 30.52) * mm, "end": v(18, 30.52) * mm});
            skLineSegment(sketch, "E84.top", {"start": v(15.16, 28.5) * mm, "end": v(18, 28.5) * mm});
            skLineSegment(sketch, "E84.left", {"start": v(15.16, 30.52) * mm, "end": v(15.16, 28.5) * mm});
            skLineSegment(sketch, "E84.right", {"start": v(18, 30.52) * mm, "end": v(18, 28.5) * mm});
            skLineSegment(sketch, "E85.trimOffspring", {"start": v(-24.5, -28.53) * mm, "end": v(-24.5, -27.68) * mm});
            skLineSegment(sketch, "E86.bottom", {"start": v(14.96, -20.57) * mm, "end": v(20.04, -20.57) * mm});
            skLineSegment(sketch, "E86.left", {"start": v(14.96, -20.57) * mm, "end": v(14.96, -18.72) * mm});
            skLineSegment(sketch, "E86.right", {"start": v(20.04, -20.57) * mm, "end": v(20.04, -18.72) * mm});
            skSolve(sketch);
        }
        {
            var Q0;
            Q0=makeQuery(id+"F2.imprint","IMPRINT",FACE,{"disambiguationData":[TD([[makeQuery(id+"F2.imprint","IMPRINT",EDGE,{"derivedFrom":sQuery(id+"F2.wireOp",EDGE,"E59.bottom")}),-1.0]])]});
            var Q1;
            Q1=makeQuery(id+"F2.imprint","IMPRINT",FACE,{"disambiguationData":[TD([[makeQuery(id+"F2.imprint","IMPRINT",EDGE,{"derivedFrom":sQuery(id+"F2.wireOp",EDGE,"E58.bottom")}),-1.0]])]});
            var Q2;
            Q2=makeQuery(id+"F2.imprint","IMPRINT",FACE,{"disambiguationData":[TD([[makeQuery(id+"F2.imprint","IMPRINT",EDGE,{"derivedFrom":sQuery(id+"F2.wireOp",EDGE,"E55.bottom")}),-1.0]])]});
            var Q3;
            {var subQ7=sQuery(id+"F2.wireOp",EDGE,"E56.bottom");Q3=makeQuery(id+"F2.imprint","IMPRINT",FACE,{"disambiguationData":[TD([[makeQuery(id+"F2.imprint","IMPRINT",EDGE,{"derivedFrom":subQ7}),1.0]])]});}
            var Q4;
            Q4=makeQuery(id+"F2.imprint","IMPRINT",FACE,{"disambiguationData":[TD([[makeQuery(id+"F2.imprint","IMPRINT",EDGE,{"derivedFrom":sQuery(id+"F2.wireOp",EDGE,"E76.bottom")}),1.0]])]});
            var Q5;
            Q5=makeQuery(id+"F2.imprint","IMPRINT",FACE,{"disambiguationData":[TD([[makeQuery(id+"F2.imprint","IMPRINT",EDGE,{"derivedFrom":sQuery(id+"F2.wireOp",EDGE,"E75.bottom")}),1.0]])]});
            var Q6;
            Q6=makeQuery(id+"F2.imprint","IMPRINT",FACE,{"disambiguationData":[TD([[makeQuery(id+"F2.imprint","IMPRINT",EDGE,{"derivedFrom":sQuery(id+"F2.wireOp",EDGE,"E53.bottom")}),1.0]])]});
            var Q7;
            {var subQ3=sQuery(id+"F2.wireOp",EDGE,"E54.bottom");Q7=makeQuery(id+"F2.imprint","IMPRINT",FACE,{"disambiguationData":[TD([[makeQuery(id+"F2.imprint","IMPRINT",EDGE,{"derivedFrom":subQ3}),1.0]])]});}
            var Q8;
            {var subQ0=sQuery(id+"F2.wireOp",EDGE,"E52.bottom");Q8=makeQuery(id+"F2.imprint","IMPRINT",FACE,{"disambiguationData":[TD([[makeQuery(id+"F2.imprint","IMPRINT",EDGE,{"derivedFrom":subQ0}),1.0]])]});}
            var Q9;
            {var subQ0=sQuery(id+"F2.wireOp",EDGE,"E32.top");Q9=makeQuery(id+"F2.imprint","IMPRINT",FACE,{"disambiguationData":[TD([[makeQuery(id+"F2.imprint","IMPRINT",EDGE,{"derivedFrom":subQ0}),-1.0]])]});}
            var Q10;
            {var subQ6=sQuery(id+"F2.wireOp",EDGE,"E32.bottom");Q10=makeQuery(id+"F2.imprint","IMPRINT",FACE,{"disambiguationData":[TD([[makeQuery(id+"F2.imprint","IMPRINT",EDGE,{"derivedFrom":subQ6}),-1.0]])]});}
            var Q11;
            Q11=makeQuery(id+"F2.imprint","IMPRINT",FACE,{"disambiguationData":[TD([[makeQuery(id+"F2.imprint","IMPRINT",EDGE,{"derivedFrom":sQuery(id+"F2.wireOp",EDGE,"E17.bottom")}),-1.0]])]});
            var Q12;
            Q12=makeQuery(id+"F2.imprint","IMPRINT",FACE,{"disambiguationData":[TD([[makeQuery(id+"F2.imprint","IMPRINT",EDGE,{"derivedFrom":sQuery(id+"F2.wireOp",EDGE,"E12.bottom")}),-1.0]])]});
            var Q13;
            Q13=makeQuery(id+"F2.imprint","IMPRINT",FACE,{"disambiguationData":[TD([[makeQuery(id+"F2.imprint","IMPRINT",EDGE,{"derivedFrom":sQuery(id+"F2.wireOp",EDGE,"E2.bottom")}),-1.0]])]});
            var Q14;
            Q14=makeQuery(id+"F2.imprint","IMPRINT",FACE,{"disambiguationData":[TD([[makeQuery(id+"F2.imprint","IMPRINT",EDGE,{"derivedFrom":sQuery(id+"F2.wireOp",EDGE,"E1.bottom")}),-1.0]])]});
            var Q15;
            Q15=makeQuery(id+"F2.imprint","IMPRINT",FACE,{"disambiguationData":[TD([[makeQuery(id+"F2.imprint","IMPRINT",EDGE,{"derivedFrom":sQuery(id+"F2.wireOp",EDGE,"E80.bottom")}),-1.0]])]});
            var Q16;
            Q16=makeQuery(id+"F2.imprint","IMPRINT",FACE,{"disambiguationData":[TD([[makeQuery(id+"F2.imprint","IMPRINT",EDGE,{"derivedFrom":sQuery(id+"F2.wireOp",EDGE,"E57.bottom")}),1.0]])]});
            var Q17;
            Q17=makeQuery(id+"F2.imprint","IMPRINT",FACE,{"disambiguationData":[TD([[makeQuery(id+"F2.imprint","IMPRINT",EDGE,{"derivedFrom":sQuery(id+"F2.wireOp",EDGE,"E63.bottom")}),-1.0]])]});
            var Q18;
            Q18=makeQuery(id+"F2.imprint","IMPRINT",FACE,{"disambiguationData":[TD([[makeQuery(id+"F2.imprint","IMPRINT",EDGE,{"derivedFrom":sQuery(id+"F2.wireOp",EDGE,"E65.bottom")}),1.0]])]});
            var Q19;
            Q19=makeQuery(id+"F2.imprint","IMPRINT",FACE,{"disambiguationData":[TD([[makeQuery(id+"F2.imprint","IMPRINT",EDGE,{"derivedFrom":sQuery(id+"F2.wireOp",EDGE,"E64.bottom")}),1.0]])]});
            var Q20;
            Q20=makeQuery(id+"F2.imprint","IMPRINT",FACE,{"disambiguationData":[TD([[makeQuery(id+"F2.imprint","IMPRINT",EDGE,{"derivedFrom":sQuery(id+"F2.wireOp",EDGE,"E66.bottom")}),1.0]])]});
            var Q21;
            Q21=makeQuery(id+"F2.imprint","IMPRINT",FACE,{"disambiguationData":[TD([[makeQuery(id+"F2.imprint","IMPRINT",EDGE,{"derivedFrom":sQuery(id+"F2.wireOp",EDGE,"E72.bottom")}),-1.0]])]});
            var Q22;
            Q22=makeQuery(id+"F2.imprint","IMPRINT",FACE,{"disambiguationData":[TD([[makeQuery(id+"F2.imprint","IMPRINT",EDGE,{"derivedFrom":sQuery(id+"F2.wireOp",EDGE,"E74.top")}),1.0]])]});
            var Q23;
            Q23=makeQuery(id+"F2.imprint","IMPRINT",FACE,{"disambiguationData":[TD([[makeQuery(id+"F2.imprint","IMPRINT",EDGE,{"derivedFrom":sQuery(id+"F2.wireOp",EDGE,"E79.bottom")}),1.0]])]});
            var Q24;
            {var subQ3=sQuery(id+"F2.wireOp",EDGE,"E4.bottom");Q24=makeQuery(id+"F2.imprint","IMPRINT",FACE,{"disambiguationData":[TD([[makeQuery(id+"F2.imprint","IMPRINT",EDGE,{"derivedFrom":subQ3}),1.0]])]});}
            var Q25;
            Q25=makeQuery(id+"F2.imprint","IMPRINT",FACE,{"disambiguationData":[TD([[makeQuery(id+"F2.imprint","IMPRINT",EDGE,{"derivedFrom":sQuery(id+"F2.wireOp",EDGE,"E10.bottom")}),-1.0]])]});
            var Q26;
            {var subQ6=sQuery(id+"F2.wireOp",EDGE,"E3.bottom");Q26=makeQuery(id+"F2.imprint","IMPRINT",FACE,{"disambiguationData":[TD([[makeQuery(id+"F2.imprint","IMPRINT",EDGE,{"derivedFrom":subQ6}),-1.0]])]});}
            var Q27;
            Q27=makeQuery(id+"F2.imprint","IMPRINT",FACE,{"disambiguationData":[TD([[makeQuery(id+"F2.imprint","IMPRINT",EDGE,{"derivedFrom":sQuery(id+"F2.wireOp",EDGE,"E77.bottom")}),1.0]])]});
            var Q28;
            Q28=makeQuery(id+"F2.imprint","IMPRINT",FACE,{"disambiguationData":[TD([[makeQuery(id+"F2.imprint","IMPRINT",EDGE,{"derivedFrom":sQuery(id+"F2.wireOp",EDGE,"E69.bottom")}),1.0]])]});
            var Q29;
            Q29=makeQuery(id+"F2.imprint","IMPRINT",FACE,{"disambiguationData":[TD([[makeQuery(id+"F2.imprint","IMPRINT",EDGE,{"derivedFrom":sQuery(id+"F2.wireOp",EDGE,"E78.bottom")}),1.0]])]});
            var Q30;
            {var subQ3=sQuery(id+"F2.wireOp",EDGE,"E70.bottom");Q30=makeQuery(id+"F2.imprint","IMPRINT",FACE,{"disambiguationData":[TD([[makeQuery(id+"F2.imprint","IMPRINT",EDGE,{"derivedFrom":subQ3}),1.0]])]});}
            var Q31;
            Q31=makeQuery(id+"F2.imprint","IMPRINT",FACE,{"disambiguationData":[TD([[makeQuery(id+"F2.imprint","IMPRINT",EDGE,{"derivedFrom":sQuery(id+"F2.wireOp",EDGE,"E73.bottom")}),1.0]])]});
            var Q32;
            Q32=makeQuery(id+"F2.imprint","IMPRINT",FACE,{"disambiguationData":[TD([[makeQuery(id+"F2.imprint","IMPRINT",EDGE,{"derivedFrom":sQuery(id+"F2.wireOp",EDGE,"E81.bottom")}),1.0]])]});
            var Q33;
            Q33=makeQuery(id+"F2.imprint","IMPRINT",FACE,{"disambiguationData":[TD([[makeQuery(id+"F2.imprint","IMPRINT",EDGE,{"derivedFrom":sQuery(id+"F2.wireOp",EDGE,"E71.bottom")}),1.0]])]});
            var Q34;
            Q34=makeQuery(id+"F2.imprint","IMPRINT",FACE,{"disambiguationData":[TD([[makeQuery(id+"F2.imprint","IMPRINT",EDGE,{"derivedFrom":sQuery(id+"F2.wireOp",EDGE,"E67.bottom")}),1.0]])]});
            var Q35;
            Q35=makeQuery(id+"F2.imprint","IMPRINT",FACE,{"disambiguationData":[TD([[makeQuery(id+"F2.imprint","IMPRINT",EDGE,{"derivedFrom":sQuery(id+"F2.wireOp",EDGE,"E68.bottom")}),1.0]])]});
            var Q36;
            Q36=makeQuery(id+"F2.imprint","IMPRINT",FACE,{"disambiguationData":[TD([[makeQuery(id+"F2.imprint","IMPRINT",EDGE,{"derivedFrom":sQuery(id+"F2.wireOp",EDGE,"E62.bottom")}),1.0]])]});
            var Q37;
            Q37=makeQuery(id+"F2.imprint","IMPRINT",FACE,{"disambiguationData":[TD([[makeQuery(id+"F2.imprint","IMPRINT",EDGE,{"derivedFrom":sQuery(id+"F2.wireOp",EDGE,"E9.bottom")}),-1.0]])]});
            var Q38;
            Q38=makeQuery(id+"F2.imprint","IMPRINT",FACE,{"disambiguationData":[TD([[makeQuery(id+"F2.imprint","IMPRINT",EDGE,{"derivedFrom":sQuery(id+"F2.wireOp",EDGE,"E8.bottom")}),1.0]])]});
            var Q39;
            Q39=makeQuery(id+"F2.imprint","IMPRINT",FACE,{"disambiguationData":[TD([[makeQuery(id+"F2.imprint","IMPRINT",EDGE,{"derivedFrom":sQuery(id+"F2.wireOp",EDGE,"E7.bottom")}),-1.0]])]});
            var Q40;
            Q40=makeQuery(id+"F2.imprint","IMPRINT",FACE,{"disambiguationData":[TD([[makeQuery(id+"F2.imprint","IMPRINT",EDGE,{"derivedFrom":sQuery(id+"F2.wireOp",EDGE,"E6.bottom")}),-1.0]])]});
            var Q41;
            Q41=makeQuery(id+"F2.imprint","IMPRINT",FACE,{"disambiguationData":[TD([[makeQuery(id+"F2.imprint","IMPRINT",EDGE,{"derivedFrom":sQuery(id+"F2.wireOp",EDGE,"E5.bottom")}),-1.0]])]});
            var Q42;
            Q42=makeQuery(id+"F2.imprint","IMPRINT",FACE,{"disambiguationData":[TD([[makeQuery(id+"F2.imprint","IMPRINT",EDGE,{"derivedFrom":sQuery(id+"F2.wireOp",EDGE,"E14.bottom")}),1.0]])]});
            var Q43;
            Q43=makeQuery(id+"F2.imprint","IMPRINT",FACE,{"disambiguationData":[TD([[makeQuery(id+"F2.imprint","IMPRINT",EDGE,{"derivedFrom":sQuery(id+"F2.wireOp",EDGE,"E13.bottom")}),1.0]])]});
            var Q44;
            {var subQ6=sQuery(id+"F2.wireOp",EDGE,"E18.bottom");Q44=makeQuery(id+"F2.imprint","IMPRINT",FACE,{"disambiguationData":[TD([[makeQuery(id+"F2.imprint","IMPRINT",EDGE,{"derivedFrom":subQ6}),1.0]])]});}
            var Q45;
            Q45=makeQuery(id+"F2.imprint","IMPRINT",FACE,{"disambiguationData":[TD([[makeQuery(id+"F2.imprint","IMPRINT",EDGE,{"derivedFrom":sQuery(id+"F2.wireOp",EDGE,"E19.bottom")}),-1.0]])]});
            var Q46;
            Q46=makeQuery(id+"F2.imprint","IMPRINT",FACE,{"disambiguationData":[TD([[makeQuery(id+"F2.imprint","IMPRINT",EDGE,{"derivedFrom":sQuery(id+"F2.wireOp",EDGE,"E15.bottom")}),-1.0]])]});
            var Q47;
            Q47=makeQuery(id+"F2.imprint","IMPRINT",FACE,{"disambiguationData":[TD([[makeQuery(id+"F2.imprint","IMPRINT",EDGE,{"derivedFrom":sQuery(id+"F2.wireOp",EDGE,"E16.bottom")}),1.0]])]});
            var Q48;
            {var subQ1=sQuery(id+"F2.wireOp",EDGE,"E11.bottom");Q48=makeQuery(id+"F2.imprint","IMPRINT",FACE,{"disambiguationData":[TD([[makeQuery(id+"F2.imprint","IMPRINT",EDGE,{"derivedFrom":subQ1}),-1.0]])]});}
            var Q49;
            {var subQ5=sQuery(id+"F2.wireOp",EDGE,"E31.right");Q49=makeQuery(id+"F2.imprint","IMPRINT",FACE,{"disambiguationData":[TD([[makeQuery(id+"F2.imprint","IMPRINT",EDGE,{"derivedFrom":subQ5}),1.0]])]});}
            var Q50;
            Q50=makeQuery(id+"F2.imprint","IMPRINT",FACE,{"disambiguationData":[TD([[makeQuery(id+"F2.imprint","IMPRINT",EDGE,{"derivedFrom":sQuery(id+"F2.wireOp",EDGE,"E29.bottom")}),1.0]])]});
            var Q51;
            Q51=makeQuery(id+"F2.imprint","IMPRINT",FACE,{"disambiguationData":[TD([[makeQuery(id+"F2.imprint","IMPRINT",EDGE,{"derivedFrom":sQuery(id+"F2.wireOp",EDGE,"E27.bottom")}),1.0]])]});
            var Q52;
            Q52=makeQuery(id+"F2.imprint","IMPRINT",FACE,{"disambiguationData":[TD([[makeQuery(id+"F2.imprint","IMPRINT",EDGE,{"derivedFrom":sQuery(id+"F2.wireOp",EDGE,"E20.bottom")}),1.0]])]});
            var Q53;
            Q53=makeQuery(id+"F2.imprint","IMPRINT",FACE,{"disambiguationData":[TD([[makeQuery(id+"F2.imprint","IMPRINT",EDGE,{"derivedFrom":sQuery(id+"F2.wireOp",EDGE,"E34.bottom")}),1.0]])]});
            var Q54;
            Q54=makeQuery(id+"F2.imprint","IMPRINT",FACE,{"disambiguationData":[TD([[makeQuery(id+"F2.imprint","IMPRINT",EDGE,{"derivedFrom":sQuery(id+"F2.wireOp",EDGE,"E36.bottom")}),-1.0]])]});
            var Q55;
            Q55=makeQuery(id+"F2.imprint","IMPRINT",FACE,{"disambiguationData":[TD([[makeQuery(id+"F2.imprint","IMPRINT",EDGE,{"derivedFrom":sQuery(id+"F2.wireOp",EDGE,"E38.bottom")}),-1.0]])]});
            var Q56;
            Q56=makeQuery(id+"F2.imprint","IMPRINT",FACE,{"disambiguationData":[TD([[makeQuery(id+"F2.imprint","IMPRINT",EDGE,{"derivedFrom":sQuery(id+"F2.wireOp",EDGE,"E40.bottom")}),1.0]])]});
            var Q57;
            Q57=makeQuery(id+"F2.imprint","IMPRINT",FACE,{"disambiguationData":[TD([[makeQuery(id+"F2.imprint","IMPRINT",EDGE,{"derivedFrom":sQuery(id+"F2.wireOp",EDGE,"E42.bottom")}),-1.0]])]});
            var Q58;
            Q58=makeQuery(id+"F2.imprint","IMPRINT",FACE,{"disambiguationData":[TD([[makeQuery(id+"F2.imprint","IMPRINT",EDGE,{"derivedFrom":sQuery(id+"F2.wireOp",EDGE,"E51.bottom")}),1.0]])]});
            var Q59;
            {var subQ5=sQuery(id+"F2.wireOp",EDGE,"E31.left");Q59=makeQuery(id+"F2.imprint","IMPRINT",FACE,{"disambiguationData":[TD([[makeQuery(id+"F2.imprint","IMPRINT",EDGE,{"derivedFrom":subQ5}),-1.0]])]});}
            var Q60;
            Q60=makeQuery(id+"F2.imprint","IMPRINT",FACE,{"disambiguationData":[TD([[makeQuery(id+"F2.imprint","IMPRINT",EDGE,{"derivedFrom":sQuery(id+"F2.wireOp",EDGE,"E47.bottom")}),1.0]])]});
            var Q61;
            Q61=makeQuery(id+"F2.imprint","IMPRINT",FACE,{"disambiguationData":[TD([[makeQuery(id+"F2.imprint","IMPRINT",EDGE,{"derivedFrom":sQuery(id+"F2.wireOp",EDGE,"E84.top")}),1.0]])]});
            var Q62;
            Q62=makeQuery(id+"F2.imprint","IMPRINT",FACE,{"disambiguationData":[TD([[makeQuery(id+"F2.imprint","IMPRINT",EDGE,{"derivedFrom":sQuery(id+"F2.wireOp",EDGE,"E44.top")}),1.0]])]});
            var Q63;
            Q63=makeQuery(id+"F2.imprint","IMPRINT",FACE,{"disambiguationData":[TD([[makeQuery(id+"F2.imprint","IMPRINT",EDGE,{"derivedFrom":sQuery(id+"F2.wireOp",EDGE,"E45.bottom")}),-1.0]])]});
            var Q64;
            Q64=makeQuery(id+"F2.imprint","IMPRINT",FACE,{"disambiguationData":[TD([[makeQuery(id+"F2.imprint","IMPRINT",EDGE,{"derivedFrom":sQuery(id+"F2.wireOp",EDGE,"E46.bottom")}),1.0]])]});
            var Q65;
            Q65=makeQuery(id+"F2.imprint","IMPRINT",FACE,{"disambiguationData":[TD([[makeQuery(id+"F2.imprint","IMPRINT",EDGE,{"derivedFrom":sQuery(id+"F2.wireOp",EDGE,"E43.bottom")}),-1.0]])]});
            var Q66;
            Q66=makeQuery(id+"F2.imprint","IMPRINT",FACE,{"disambiguationData":[TD([[makeQuery(id+"F2.imprint","IMPRINT",EDGE,{"derivedFrom":sQuery(id+"F2.wireOp",EDGE,"E49.bottom")}),-1.0]])]});
            var Q67;
            Q67=makeQuery(id+"F2.imprint","IMPRINT",FACE,{"disambiguationData":[TD([[makeQuery(id+"F2.imprint","IMPRINT",EDGE,{"derivedFrom":sQuery(id+"F2.wireOp",EDGE,"E86.bottom")}),1.0]])]});
            var Q68;
            {var subQ3=sQuery(id+"F2.wireOp",EDGE,"E21.right");Q68=makeQuery(id+"F2.imprint","IMPRINT",FACE,{"disambiguationData":[TD([[makeQuery(id+"F2.imprint","IMPRINT",EDGE,{"derivedFrom":subQ3}),1.0]])]});}
            var Q69;
            Q69=makeQuery(id+"F2.imprint","IMPRINT",FACE,{"disambiguationData":[TD([[makeQuery(id+"F2.imprint","IMPRINT",EDGE,{"derivedFrom":sQuery(id+"F2.wireOp",EDGE,"E50.bottom")}),-1.0]])]});
            var Q70;
            {var subQ4=sQuery(id+"F2.wireOp",EDGE,"E22.top");Q70=makeQuery(id+"F2.imprint","IMPRINT",FACE,{"disambiguationData":[TD([[makeQuery(id+"F2.imprint","IMPRINT",EDGE,{"derivedFrom":subQ4}),-1.0]])]});}
            var Q71;
            Q71=makeQuery(id+"F2.imprint","IMPRINT",FACE,{"disambiguationData":[TD([[makeQuery(id+"F2.imprint","IMPRINT",EDGE,{"derivedFrom":sQuery(id+"F2.wireOp",EDGE,"E48.bottom")}),1.0]])]});
            var Q72;
            Q72=makeQuery(id+"F2.imprint","IMPRINT",FACE,{"disambiguationData":[TD([[makeQuery(id+"F2.imprint","IMPRINT",EDGE,{"derivedFrom":sQuery(id+"F2.wireOp",EDGE,"E23.bottom")}),-1.0]])]});
            var Q73;
            {var subQ1=sQuery(id+"F2.wireOp",EDGE,"E24.bottom");Q73=makeQuery(id+"F2.imprint","IMPRINT",FACE,{"disambiguationData":[TD([[makeQuery(id+"F2.imprint","IMPRINT",EDGE,{"derivedFrom":subQ1}),1.0]])]});}
            var Q74;
            {var subQ5=sQuery(id+"F2.wireOp",EDGE,"E30.left");Q74=makeQuery(id+"F2.imprint","IMPRINT",FACE,{"disambiguationData":[TD([[makeQuery(id+"F2.imprint","IMPRINT",EDGE,{"derivedFrom":subQ5}),1.0]])]});}
            var Q75;
            {var subQ5=sQuery(id+"F2.wireOp",EDGE,"E30.right");Q75=makeQuery(id+"F2.imprint","IMPRINT",FACE,{"disambiguationData":[TD([[makeQuery(id+"F2.imprint","IMPRINT",EDGE,{"derivedFrom":subQ5}),-1.0]])]});}
            var Q76;
            Q76=makeQuery(id+"F2.imprint","IMPRINT",FACE,{"disambiguationData":[TD([[makeQuery(id+"F2.imprint","IMPRINT",EDGE,{"derivedFrom":sQuery(id+"F2.wireOp",EDGE,"E28.bottom")}),-1.0]])]});
            var Q77;
            Q77=makeQuery(id+"F2.imprint","IMPRINT",FACE,{"disambiguationData":[TD([[makeQuery(id+"F2.imprint","IMPRINT",EDGE,{"derivedFrom":sQuery(id+"F2.wireOp",EDGE,"E26.bottom")}),-1.0]])]});
            var Q78;
            Q78=makeQuery(id+"F2.imprint","IMPRINT",FACE,{"disambiguationData":[TD([[makeQuery(id+"F2.imprint","IMPRINT",EDGE,{"derivedFrom":sQuery(id+"F2.wireOp",EDGE,"E25.bottom")}),-1.0]])]});
            var Q79;
            Q79=makeQuery(id+"F2.imprint","IMPRINT",FACE,{"disambiguationData":[TD([[makeQuery(id+"F2.imprint","IMPRINT",EDGE,{"derivedFrom":sQuery(id+"F2.wireOp",EDGE,"E41.bottom")}),1.0]])]});
            var Q80;
            Q80=makeQuery(id+"F2.imprint","IMPRINT",FACE,{"disambiguationData":[TD([[makeQuery(id+"F2.imprint","IMPRINT",EDGE,{"derivedFrom":sQuery(id+"F2.wireOp",EDGE,"E39.bottom")}),1.0]])]});
            var Q81;
            Q81=makeQuery(id+"F2.imprint","IMPRINT",FACE,{"disambiguationData":[TD([[makeQuery(id+"F2.imprint","IMPRINT",EDGE,{"derivedFrom":sQuery(id+"F2.wireOp",EDGE,"E37.bottom")}),1.0]])]});
            var Q82;
            Q82=makeQuery(id+"F2.imprint","IMPRINT",FACE,{"disambiguationData":[TD([[makeQuery(id+"F2.imprint","IMPRINT",EDGE,{"derivedFrom":sQuery(id+"F2.wireOp",EDGE,"E35.bottom")}),1.0]])]});
            extrude(context, id + "F3", {"entities" : qUnion([Q0, Q1, Q2, Q3, Q4, Q5, Q6, Q7, Q8, Q9, Q10, Q11, Q12, Q13, Q14, Q15, Q16, Q17, Q18, Q19, Q20, Q21, Q22, Q23, Q24, Q25, Q26, Q27, Q28, Q29, Q30, Q31, Q32, Q33, Q34, Q35, Q36, Q37, Q38, Q39, Q40, Q41, Q42, Q43, Q44, Q45, Q46, Q47, Q48, Q49, Q50, Q51, Q52, Q53, Q54, Q55, Q56, Q57, Q58, Q59, Q60, Q61, Q62, Q63, Q64, Q65, Q66, Q67, Q68, Q69, Q70, Q71, Q72, Q73, Q74, Q75, Q76, Q77, Q78, Q79, Q80, Q81, Q82]), "operationType" : NewBodyOperationType.ADD, "depth" : 10 * mm});
        }
    });
